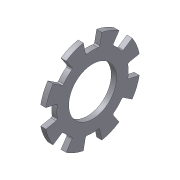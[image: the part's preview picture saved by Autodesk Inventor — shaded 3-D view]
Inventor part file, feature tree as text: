
AUTODESK INVENTOR PART (.ipt)
format: ipt  version: 2014 (Build 180170000, 170)  size: 133,120 bytes
history: native  units: mm (DEFAULTED — no unit token found)
features: sketch x2, extrude x1, pattern_circular x1
ambient origin geometry x8: Origin, YZ Plane, XZ Plane, XY Plane, X Axis, Y Axis, Z Axis, Center Point
bodies: Solid1 (feature_tree), Body (feature_tree)
feature tree (4):
  extrude  "Cut"  Depth=6.5024mm
  pattern_circular  "Cuts"  [2 undecoded]
  sketch  "Sketch1"  dims[d0=12.954mm d1=6.5024mm]
  sketch  "Sketch2"  dims[d2=0.7112mm d3=0.0mm d4=22.5deg d5=9.7282mm d6=0.7112mm d7=0.0mm d8=0.19431mm d9=80.0mm d11=360.0deg d12=0.0mm d13=0.0mm]
note: 2 required parameter values undecoded (feature->parameter linkage not recoverable at this tier; creation-order binding heuristic only, values carry confidence <= 0.55)
